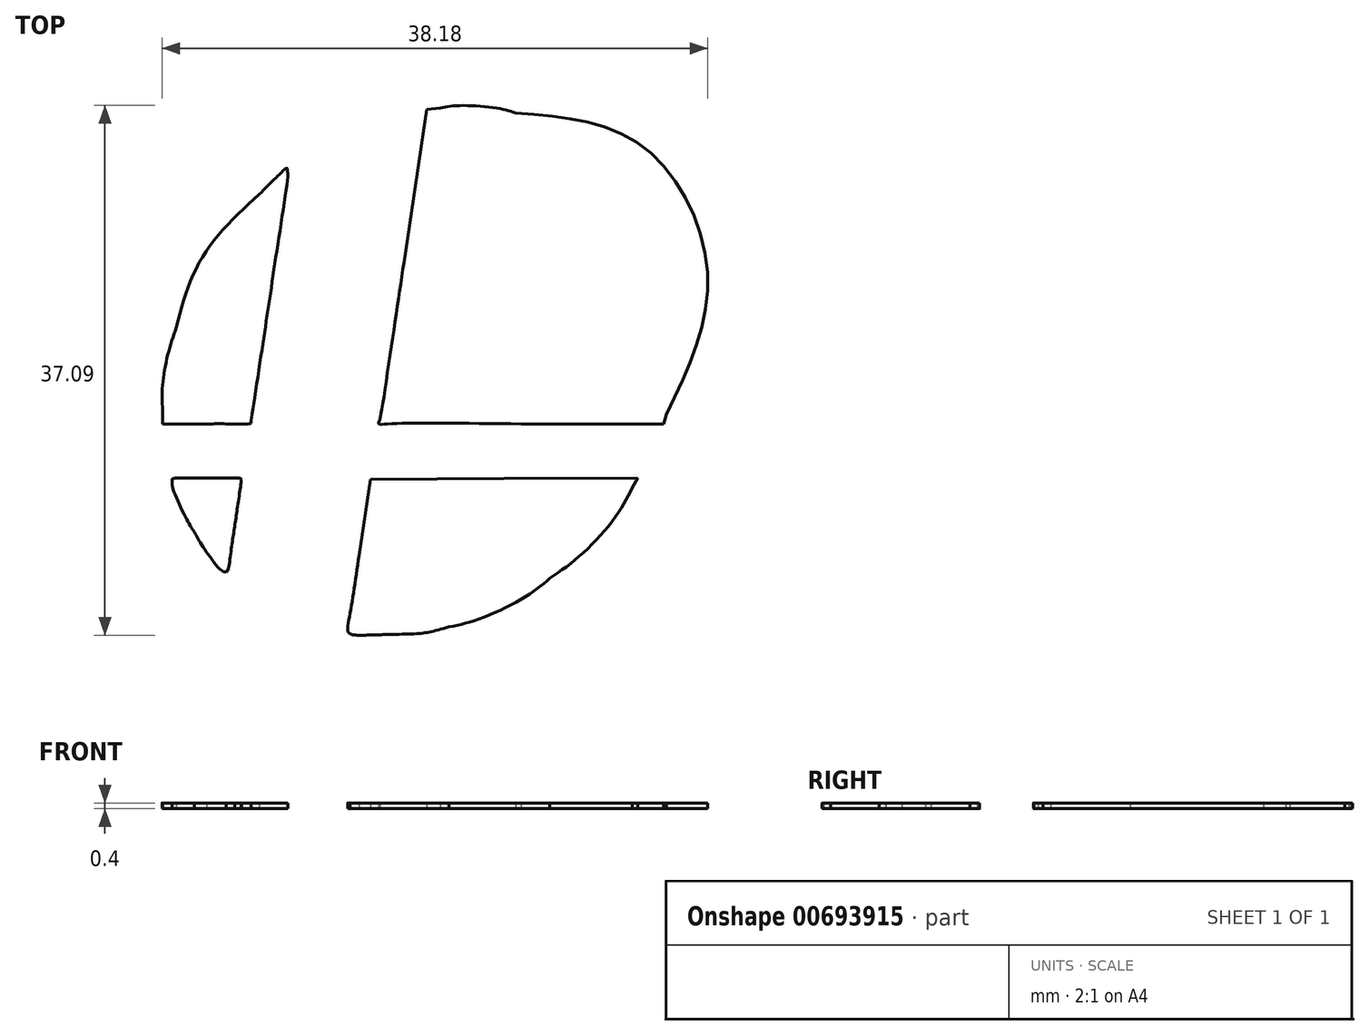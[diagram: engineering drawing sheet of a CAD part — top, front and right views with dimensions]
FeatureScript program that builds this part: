
annotation { "Feature Type Name" : "Feature", "Feature Type Description" : "" }
export const myFeature = defineFeature(function(context is Context, id is Id, definition is map)
    precondition{}
    {
        {
            var Q0;
            Q0=qCreatedBy(makeId("Top.planeOp"),FACE);
            var sketch = newSketch(context, id + "F0", { "sketchPlane" : qUnion([Q0])});
            skFitSpline(sketch, "E0", {"points": [v(-1.5, -38.66) * mm, v(-1.62, -38.6) * mm, v(-1.86, -38.27) * mm, v(-2.05, -37.9) * mm]});
            skFitSpline(sketch, "E1", {"points": [v(-2.05, -37.9) * mm, v(-2.61, -36.8) * mm, v(-4.04, -36.4) * mm, v(-5.38, -36.95) * mm]});
            skFitSpline(sketch, "E2", {"points": [v(-5.38, -36.95) * mm, v(-6.21, -37.3) * mm, v(-7.38, -37.27) * mm, v(-8.93, -36.87) * mm]});
            skFitSpline(sketch, "E3", {"points": [v(-8.93, -36.87) * mm, v(-9.64, -36.68) * mm, v(-10.67, -36.53) * mm, v(-11.21, -36.53) * mm]});
            skFitSpline(sketch, "E4", {"points": [v(-12.1, -36) * mm, v(-11.96, -35.34) * mm, v(-12.11, -35.34) * mm, v(-14.25, -36) * mm]});
            skFitSpline(sketch, "E5", {"points": [v(-14.25, -36) * mm, v(-16.51, -36.7) * mm, v(-18.19, -36.93) * mm, v(-20, -36.8) * mm]});
            skFitSpline(sketch, "E6", {"points": [v(-20, -36.8) * mm, v(-21.86, -36.67) * mm, v(-23.16, -36.25) * mm, v(-24.98, -35.16) * mm]});
            skFitSpline(sketch, "E7", {"points": [v(-24.98, -35.16) * mm, v(-25.76, -34.7) * mm, v(-26.77, -34.22) * mm, v(-27.22, -34.1) * mm]});
            skFitSpline(sketch, "E8", {"points": [v(-27.22, -34.1) * mm, v(-28.1, -33.89) * mm, v(-28.19, -33.77) * mm, v(-27.78, -33.43) * mm]});
            skFitSpline(sketch, "E9", {"points": [v(-27.78, -33.43) * mm, v(-27.64, -33.3) * mm, v(-27.52, -33.16) * mm, v(-27.52, -33.1) * mm]});
            skFitSpline(sketch, "E10", {"points": [v(-27.52, -33.1) * mm, v(-27.52, -33.02) * mm, v(-28.28, -32.84) * mm, v(-29.22, -32.69) * mm]});
            skFitSpline(sketch, "E11", {"points": [v(-29.22, -32.69) * mm, v(-31.36, -32.34) * mm, v(-32.5, -31.83) * mm, v(-33.76, -30.68) * mm]});
            skFitSpline(sketch, "E12", {"points": [v(-33.76, -30.68) * mm, v(-35.5, -29.09) * mm, v(-36.12, -27.5) * mm, v(-35.53, -26.12) * mm]});
            skFitSpline(sketch, "E13", {"points": [v(-35.53, -26.12) * mm, v(-35.27, -25.47) * mm, v(-35.27, -25.42) * mm, v(-35.58, -25) * mm]});
            skFitSpline(sketch, "E14", {"points": [v(-35.58, -25) * mm, v(-36.12, -24.27) * mm, v(-36.64, -23.14) * mm, v(-36.64, -22.72) * mm]});
            skFitSpline(sketch, "E15", {"points": [v(-36.64, -22.72) * mm, v(-36.64, -22.5) * mm, v(-36.52, -22.15) * mm, v(-36.37, -21.93) * mm]});
            skFitSpline(sketch, "E16", {"points": [v(-36.37, -21.93) * mm, v(-36.03, -21.45) * mm, v(-36.13, -21.3) * mm, v(-37.15, -20.78) * mm]});
            skFitSpline(sketch, "E17", {"points": [v(-37.15, -20.78) * mm, v(-38.12, -20.29) * mm, v(-39, -19.3) * mm, v(-39.22, -18.45) * mm]});
            skFitSpline(sketch, "E18", {"points": [v(-39.22, -18.45) * mm, v(-39.36, -17.88) * mm, v(-39.67, -15.62) * mm, v(-39.85, -13.7) * mm]});
            skLineSegment(sketch, "E19", {"start": v(-11.21, -36.53) * mm, "end": v(-12.2, -36.52) * mm});
            skLineSegment(sketch, "E20", {"start": v(-12.2, -36.52) * mm, "end": v(-12.1, -36) * mm});
            skFitSpline(sketch, "E21", {"points": [v(-39.4, -12.9) * mm, v(-38.76, -13) * mm, v(-38.4, -12.74) * mm, v(-38.22, -12.03) * mm]});
            skFitSpline(sketch, "E22", {"points": [v(-38.22, -12.03) * mm, v(-38.1, -11.58) * mm, v(-37.97, -11.47) * mm, v(-37.4, -11.36) * mm]});
            skFitSpline(sketch, "E23", {"points": [v(-37.4, -11.36) * mm, v(-36.15, -11.1) * mm, v(-36.04, -10.46) * mm, v(-36.72, -7.13) * mm]});
            skFitSpline(sketch, "E24", {"points": [v(-36.72, -7.13) * mm, v(-37.48, -3.42) * mm, v(-37.47, -0.76) * mm, v(-36.7, 0.41) * mm]});
            skLineSegment(sketch, "E25", {"start": v(-39.85, -13.7) * mm, "end": v(-39.94, -12.83) * mm});
            skLineSegment(sketch, "E26", {"start": v(-39.94, -12.83) * mm, "end": v(-39.4, -12.9) * mm});
            skFitSpline(sketch, "E27", {"points": [v(-36.25, 0.32) * mm, v(-36.14, -0.12) * mm, v(-36.03, -0.22) * mm, v(-35.73, -0.18) * mm]});
            skFitSpline(sketch, "E28", {"points": [v(-35.73, -0.18) * mm, v(-35.16, -0.1) * mm, v(-34.73, 0.95) * mm, v(-34.62, 2.55) * mm]});
            skFitSpline(sketch, "E29", {"points": [v(-34.62, 2.55) * mm, v(-34.57, 3.3) * mm, v(-34.48, 3.9) * mm, v(-34.42, 3.87) * mm]});
            skFitSpline(sketch, "E30", {"points": [v(-34.42, 3.87) * mm, v(-33.43, 3.32) * mm, v(-32.93, 3.2) * mm, v(-32.28, 3.4) * mm]});
            skFitSpline(sketch, "E31", {"points": [v(-32.28, 3.4) * mm, v(-30.88, 3.82) * mm, v(-28.76, 6.37) * mm, v(-28.4, 8.06) * mm]});
            skFitSpline(sketch, "E32", {"points": [v(-28.4, 8.06) * mm, v(-28.18, 9.04) * mm, v(-28.44, 9.93) * mm, v(-29.04, 10.3) * mm]});
            skFitSpline(sketch, "E33", {"points": [v(-29.04, 10.3) * mm, v(-29.36, 10.5) * mm, v(-29.37, 10.57) * mm, v(-29.14, 11.13) * mm]});
            skFitSpline(sketch, "E34", {"points": [v(-29.14, 11.13) * mm, v(-29.01, 11.47) * mm, v(-28.66, 12.56) * mm, v(-28.37, 13.55) * mm]});
            skFitSpline(sketch, "E35", {"points": [v(-28.37, 13.55) * mm, v(-28.08, 14.55) * mm, v(-27.62, 15.71) * mm, v(-27.34, 16.14) * mm]});
            skFitSpline(sketch, "E36", {"points": [v(-27.34, 16.14) * mm, v(-26.85, 16.9) * mm, v(-25.28, 18.56) * mm, v(-25.28, 18.31) * mm]});
            skFitSpline(sketch, "E37", {"points": [v(-25.28, 18.31) * mm, v(-25.28, 18.24) * mm, v(-25.4, 17.8) * mm, v(-25.56, 17.32) * mm]});
            skFitSpline(sketch, "E38", {"points": [v(-25.56, 17.32) * mm, v(-25.91, 16.25) * mm, v(-25.8, 15.03) * mm, v(-25.31, 14.54) * mm]});
            skFitSpline(sketch, "E39", {"points": [v(-25.31, 14.54) * mm, v(-24.47, 13.7) * mm, v(-21.96, 14.42) * mm, v(-20.69, 15.86) * mm]});
            skFitSpline(sketch, "E40", {"points": [v(-20.69, 15.86) * mm, v(-20.33, 16.27) * mm, v(-19.57, 17.49) * mm, v(-19, 18.56) * mm]});
            skFitSpline(sketch, "E41", {"points": [v(-19, 18.56) * mm, v(-17.86, 20.73) * mm, v(-16.65, 22.12) * mm, v(-15.24, 22.9) * mm]});
            skFitSpline(sketch, "E42", {"points": [v(-15.24, 22.9) * mm, v(-14.78, 23.16) * mm, v(-14.37, 23.36) * mm, v(-14.34, 23.36) * mm]});
            skFitSpline(sketch, "E43", {"points": [v(-14.34, 23.36) * mm, v(-14.3, 23.36) * mm, v(-14.44, 23.1) * mm, v(-14.63, 22.76) * mm]});
            skFitSpline(sketch, "E44", {"points": [v(-14.63, 22.76) * mm, v(-15.12, 21.94) * mm, v(-15.1, 20.92) * mm, v(-14.55, 19.56) * mm]});
            skFitSpline(sketch, "E45", {"points": [v(-14.55, 19.56) * mm, v(-14, 18.2) * mm, v(-13.98, 17.3) * mm, v(-14.45, 16.1) * mm]});
            skFitSpline(sketch, "E46", {"points": [v(-14.45, 16.1) * mm, v(-14.68, 15.54) * mm, v(-14.76, 15.05) * mm, v(-14.7, 14.77) * mm]});
            skFitSpline(sketch, "E47", {"points": [v(-14.7, 14.77) * mm, v(-14.58, 14.36) * mm, v(-14.56, 14.38) * mm, v(-14.34, 15.1) * mm]});
            skFitSpline(sketch, "E48", {"points": [v(-14.34, 15.1) * mm, v(-14.2, 15.59) * mm, v(-13.89, 16.05) * mm, v(-13.5, 16.39) * mm]});
            skFitSpline(sketch, "E49", {"points": [v(-13.5, 16.39) * mm, v(-13.15, 16.68) * mm, v(-12.77, 17.22) * mm, v(-12.63, 17.6) * mm]});
            skLineSegment(sketch, "E50", {"start": v(-36.7, 0.41) * mm, "end": v(-36.4, 0.87) * mm});
            skLineSegment(sketch, "E51", {"start": v(-36.4, 0.87) * mm, "end": v(-36.25, 0.32) * mm});
            skFitSpline(sketch, "E52", {"points": [v(-12.38, 17.11) * mm, v(-12.38, 16.46) * mm, v(-12.5, 15.46) * mm, v(-12.66, 14.87) * mm]});
            skFitSpline(sketch, "E53", {"points": [v(-12.66, 14.87) * mm, v(-13.02, 13.5) * mm, v(-12.8, 12.48) * mm, v(-12.03, 12.1) * mm]});
            skFitSpline(sketch, "E54", {"points": [v(-12.03, 12.1) * mm, v(-11.76, 11.95) * mm, v(-11.5, 11.83) * mm, v(-11.44, 11.83) * mm]});
            skFitSpline(sketch, "E55", {"points": [v(-11.44, 11.83) * mm, v(-11.39, 11.83) * mm, v(-11.34, 12.22) * mm, v(-11.34, 12.68) * mm]});
            skFitSpline(sketch, "E56", {"points": [v(-11.34, 12.68) * mm, v(-11.34, 13.78) * mm, v(-11.12, 14.35) * mm, v(-10.4, 15.05) * mm]});
            skFitSpline(sketch, "E57", {"points": [v(-10.4, 15.05) * mm, v(-9.7, 15.73) * mm, v(-9.65, 16.08) * mm, v(-9.92, 18.2) * mm]});
            skFitSpline(sketch, "E58", {"points": [v(-9.92, 18.2) * mm, v(-10.03, 19.1) * mm, v(-10.13, 20.33) * mm, v(-10.13, 20.94) * mm]});
            skFitSpline(sketch, "E59", {"points": [v(-10.13, 20.94) * mm, v(-10.14, 21.93) * mm, v(-10.07, 22.17) * mm, v(-9.46, 23.18) * mm]});
            skFitSpline(sketch, "E60", {"points": [v(-9.46, 23.18) * mm, v(-8.57, 24.68) * mm, v(-8.51, 25.02) * mm, v(-9.2, 24.94) * mm]});
            skFitSpline(sketch, "E61", {"points": [v(-9.2, 24.94) * mm, v(-9.9, 24.87) * mm, v(-10.4, 24.52) * mm, v(-11.01, 23.66) * mm]});
            skLineSegment(sketch, "E62", {"start": v(-12.63, 17.6) * mm, "end": v(-12.4, 18.29) * mm});
            skLineSegment(sketch, "E63", {"start": v(-12.4, 18.29) * mm, "end": v(-12.38, 17.11) * mm});
            skFitSpline(sketch, "E64", {"points": [v(-11.42, 24.14) * mm, v(-11.19, 26.66) * mm, v(-10.74, 27.64) * mm, v(-8.77, 29.86) * mm]});
            skFitSpline(sketch, "E65", {"points": [v(-8.77, 29.86) * mm, v(-8, 30.74) * mm, v(-7.34, 31.45) * mm, v(-7.3, 31.45) * mm]});
            skFitSpline(sketch, "E66", {"points": [v(-7.3, 31.45) * mm, v(-7.26, 31.45) * mm, v(-7.35, 31.18) * mm, v(-7.49, 30.84) * mm]});
            skFitSpline(sketch, "E67", {"points": [v(-7.49, 30.84) * mm, v(-7.63, 30.5) * mm, v(-7.7, 30.16) * mm, v(-7.64, 30.07) * mm]});
            skFitSpline(sketch, "E68", {"points": [v(-7.64, 30.07) * mm, v(-7.27, 29.47) * mm, v(-5.55, 30.5) * mm, v(-4.96, 31.67) * mm]});
            skFitSpline(sketch, "E69", {"points": [v(-4.96, 31.67) * mm, v(-4, 33.55) * mm, v(-2.7, 34.97) * mm, v(-1.21, 35.75) * mm]});
            skLineSegment(sketch, "E70", {"start": v(-11.01, 23.66) * mm, "end": v(-11.53, 22.94) * mm});
            skLineSegment(sketch, "E71", {"start": v(-11.53, 22.94) * mm, "end": v(-11.42, 24.14) * mm});
            skFitSpline(sketch, "E72", {"points": [v(-1.23, 35.39) * mm, v(-1.47, 35.07) * mm, v(-1.76, 34.62) * mm, v(-1.88, 34.4) * mm]});
            skFitSpline(sketch, "E73", {"points": [v(-1.88, 34.4) * mm, v(-2.08, 34) * mm, v(-2.07, 34) * mm, v(-1.6, 34.11) * mm]});
            skLineSegment(sketch, "E74", {"start": v(-1.21, 35.75) * mm, "end": v(-0.8, 35.96) * mm});
            skLineSegment(sketch, "E75", {"start": v(-0.8, 35.96) * mm, "end": v(-1.23, 35.39) * mm});
            skFitSpline(sketch, "E76", {"points": [v(-1.47, 33.83) * mm, v(-2.74, 32.41) * mm, v(-1.79, 32.96) * mm, v(0.05, 34.7) * mm]});
            skFitSpline(sketch, "E77", {"points": [v(0.05, 34.7) * mm, v(0.88, 35.49) * mm, v(1.75, 36.52) * mm, v(2.12, 37.15) * mm]});
            skLineSegment(sketch, "E78", {"start": v(-1.6, 34.11) * mm, "end": v(-1.1, 34.23) * mm});
            skLineSegment(sketch, "E79", {"start": v(-1.1, 34.23) * mm, "end": v(-1.47, 33.83) * mm});
            skFitSpline(sketch, "E80", {"points": [v(2.77, 36.92) * mm, v(2.77, 34.91) * mm, v(2.38, 34.08) * mm, v(0.51, 32.04) * mm]});
            skFitSpline(sketch, "E81", {"points": [v(0.51, 32.04) * mm, v(-1.75, 29.57) * mm, v(-2.86, 28.17) * mm, v(-3.24, 27.3) * mm]});
            skFitSpline(sketch, "E82", {"points": [v(-3.24, 27.3) * mm, v(-3.76, 26.12) * mm, v(-3.77, 25.43) * mm, v(-3.27, 25.43) * mm]});
            skFitSpline(sketch, "E83", {"points": [v(-3.27, 25.43) * mm, v(-2.77, 25.43) * mm, v(-2.02, 26.42) * mm, v(-1.46, 27.8) * mm]});
            skLineSegment(sketch, "E84", {"start": v(2.12, 37.15) * mm, "end": v(2.77, 38.24) * mm});
            skLineSegment(sketch, "E85", {"start": v(2.77, 38.24) * mm, "end": v(2.77, 36.92) * mm});
            skFitSpline(sketch, "E86", {"points": [v(-0.74, 28.53) * mm, v(-0.6, 28.21) * mm, v(-0.4, 28.01) * mm, v(-0.2, 28.01) * mm]});
            skFitSpline(sketch, "E87", {"points": [v(-0.2, 28.01) * mm, v(0.33, 28.01) * mm, v(1.4, 28.9) * mm, v(2.41, 30.13) * mm]});
            skFitSpline(sketch, "E88", {"points": [v(2.41, 30.13) * mm, v(2.93, 30.76) * mm, v(3.37, 31.28) * mm, v(3.4, 31.28) * mm]});
            skFitSpline(sketch, "E89", {"points": [v(3.4, 31.28) * mm, v(3.42, 31.28) * mm, v(3.25, 30.78) * mm, v(3.02, 30.16) * mm]});
            skFitSpline(sketch, "E90", {"points": [v(3.02, 30.16) * mm, v(2.56, 28.93) * mm, v(2.48, 28.25) * mm, v(2.8, 28.14) * mm]});
            skFitSpline(sketch, "E91", {"points": [v(2.8, 28.14) * mm, v(3.27, 27.99) * mm, v(1.8, 25.16) * mm, v(0.4, 23.54) * mm]});
            skFitSpline(sketch, "E92", {"points": [v(0.4, 23.54) * mm, v(0, 23.08) * mm, v(-0.98, 22.22) * mm, v(-1.78, 21.64) * mm]});
            skFitSpline(sketch, "E93", {"points": [v(-1.78, 21.64) * mm, v(-2.89, 20.84) * mm, v(-3.29, 20.43) * mm, v(-3.5, 19.9) * mm]});
            skFitSpline(sketch, "E94", {"points": [v(-3.5, 19.9) * mm, v(-3.85, 19.04) * mm, v(-3.87, 17.51) * mm, v(-3.53, 17.51) * mm]});
            skFitSpline(sketch, "E95", {"points": [v(-3.53, 17.51) * mm, v(-3.2, 17.51) * mm, v(-2.62, 18.03) * mm, v(-2.3, 18.63) * mm]});
            skLineSegment(sketch, "E96", {"start": v(-1.46, 27.8) * mm, "end": v(-0.96, 29.06) * mm});
            skLineSegment(sketch, "E97", {"start": v(-0.96, 29.06) * mm, "end": v(-0.74, 28.53) * mm});
            skFitSpline(sketch, "E98", {"points": [v(-2.12, 18.33) * mm, v(-2.23, 17.4) * mm, v(-2.5, 16.8) * mm, v(-3.38, 15.5) * mm]});
            skFitSpline(sketch, "E99", {"points": [v(-3.38, 15.5) * mm, v(-4.52, 13.82) * mm, v(-3.7, 13.38) * mm, v(-1.81, 14.68) * mm]});
            skFitSpline(sketch, "E100", {"points": [v(-1.81, 14.68) * mm, v(-0.75, 15.4) * mm, v(0.32, 15.96) * mm, v(0.65, 15.96) * mm]});
            skFitSpline(sketch, "E101", {"points": [v(0.65, 15.96) * mm, v(0.72, 15.96) * mm, v(0.5, 15.67) * mm, v(0.15, 15.32) * mm]});
            skFitSpline(sketch, "E102", {"points": [v(0.15, 15.32) * mm, v(-0.5, 14.65) * mm, v(-1.16, 13.45) * mm, v(-1.54, 12.26) * mm]});
            skFitSpline(sketch, "E103", {"points": [v(-1.54, 12.26) * mm, v(-1.86, 11.26) * mm, v(-2.58, 10.29) * mm, v(-3.9, 9.1) * mm]});
            skLineSegment(sketch, "E104", {"start": v(-2.3, 18.63) * mm, "end": v(-2.02, 19.15) * mm});
            skLineSegment(sketch, "E105", {"start": v(-2.02, 19.15) * mm, "end": v(-2.12, 18.33) * mm});
            skFitSpline(sketch, "E106", {"points": [v(-4.23, 8.39) * mm, v(-3.16, 8.84) * mm, v(-1, 10.32) * mm, v(0, 11.32) * mm]});
            skFitSpline(sketch, "E107", {"points": [v(0, 11.32) * mm, v(1.25, 12.53) * mm, v(1.9, 14.34) * mm, v(1.9, 16.53) * mm]});
            skFitSpline(sketch, "E108", {"points": [v(1.9, 16.53) * mm, v(1.9, 17) * mm, v(2, 17.7) * mm, v(2.12, 18.1) * mm]});
            skFitSpline(sketch, "E109", {"points": [v(2.12, 18.1) * mm, v(2.36, 18.92) * mm, v(3.71, 20.37) * mm, v(4.4, 20.54) * mm]});
            skFitSpline(sketch, "E110", {"points": [v(4.4, 20.54) * mm, v(4.7, 20.62) * mm, v(4.97, 20.9) * mm, v(5.26, 21.46) * mm]});
            skFitSpline(sketch, "E111", {"points": [v(5.26, 21.46) * mm, v(5.8, 22.51) * mm, v(6.7, 23.32) * mm, v(8.2, 24.06) * mm]});
            skFitSpline(sketch, "E112", {"points": [v(8.2, 24.06) * mm, v(10.3, 25.1) * mm, v(11.51, 26.57) * mm, v(12.88, 29.73) * mm]});
            skFitSpline(sketch, "E113", {"points": [v(12.88, 29.73) * mm, v(13.05, 30.1) * mm, v(13.07, 30.03) * mm, v(13.08, 29.14) * mm]});
            skFitSpline(sketch, "E114", {"points": [v(13.08, 29.14) * mm, v(13.09, 28.58) * mm, v(13, 27.63) * mm, v(12.9, 27.03) * mm]});
            skFitSpline(sketch, "E115", {"points": [v(12.9, 27.03) * mm, v(12.8, 26.42) * mm, v(12.76, 25.88) * mm, v(12.82, 25.81) * mm]});
            skFitSpline(sketch, "E116", {"points": [v(12.82, 25.81) * mm, v(12.89, 25.75) * mm, v(13.1, 25.8) * mm, v(13.32, 25.93) * mm]});
            skFitSpline(sketch, "E117", {"points": [v(13.32, 25.93) * mm, v(13.68, 26.16) * mm, v(13.69, 26.15) * mm, v(13.4, 25.83) * mm]});
            skFitSpline(sketch, "E118", {"points": [v(13.4, 25.83) * mm, v(12.94, 25.32) * mm, v(12.6, 24.36) * mm, v(12.7, 23.86) * mm]});
            skFitSpline(sketch, "E119", {"points": [v(12.7, 23.86) * mm, v(12.82, 23.19) * mm, v(12.38, 22.65) * mm, v(11.07, 21.89) * mm]});
            skFitSpline(sketch, "E120", {"points": [v(11.07, 21.89) * mm, v(9.08, 20.73) * mm, v(8.23, 19.79) * mm, v(7.92, 18.4) * mm]});
            skFitSpline(sketch, "E121", {"points": [v(7.92, 18.4) * mm, v(7.84, 18.07) * mm, v(7.86, 17.62) * mm, v(7.95, 17.38) * mm]});
            skFitSpline(sketch, "E122", {"points": [v(7.95, 17.38) * mm, v(8.1, 16.99) * mm, v(8.18, 16.96) * mm, v(8.97, 17.04) * mm]});
            skFitSpline(sketch, "E123", {"points": [v(8.97, 17.04) * mm, v(10.1, 17.14) * mm, v(10.08, 16.93) * mm, v(8.88, 16.07) * mm]});
            skFitSpline(sketch, "E124", {"points": [v(8.88, 16.07) * mm, v(8.3, 15.66) * mm, v(8.7, 15.57) * mm, v(9.77, 15.88) * mm]});
            skFitSpline(sketch, "E125", {"points": [v(9.77, 15.88) * mm, v(11.34, 16.33) * mm, v(11.77, 16.77) * mm, v(12.92, 19.05) * mm]});
            skFitSpline(sketch, "E126", {"points": [v(12.92, 19.05) * mm, v(13.47, 20.17) * mm, v(14.19, 21.33) * mm, v(14.5, 21.65) * mm]});
            skFitSpline(sketch, "E127", {"points": [v(14.5, 21.65) * mm, v(15.05, 22.2) * mm, v(16.82, 23.14) * mm, v(16.98, 22.98) * mm]});
            skFitSpline(sketch, "E128", {"points": [v(16.98, 22.98) * mm, v(17.03, 22.93) * mm, v(16.78, 22.68) * mm, v(16.44, 22.42) * mm]});
            skFitSpline(sketch, "E129", {"points": [v(16.44, 22.42) * mm, v(15.8, 21.94) * mm, v(15.16, 20.81) * mm, v(15.17, 20.18) * mm]});
            skFitSpline(sketch, "E130", {"points": [v(15.17, 20.18) * mm, v(15.17, 19.88) * mm, v(15.22, 19.9) * mm, v(15.62, 20.34) * mm]});
            skLineSegment(sketch, "E131", {"start": v(-3.9, 9.1) * mm, "end": v(-5.06, 8.04) * mm});
            skLineSegment(sketch, "E132", {"start": v(-5.06, 8.04) * mm, "end": v(-4.23, 8.39) * mm});
            skFitSpline(sketch, "E133", {"points": [v(15.94, 20.08) * mm, v(15.88, 19.66) * mm, v(15.55, 18.72) * mm, v(15.22, 17.98) * mm]});
            skFitSpline(sketch, "E134", {"points": [v(15.22, 17.98) * mm, v(14.56, 16.55) * mm, v(14.56, 16.04) * mm, v(15.2, 16.23) * mm]});
            skFitSpline(sketch, "E135", {"points": [v(15.2, 16.23) * mm, v(16.13, 16.5) * mm, v(18.1, 17.84) * mm, v(19.2, 18.96) * mm]});
            skFitSpline(sketch, "E136", {"points": [v(19.2, 18.96) * mm, v(20.48, 20.24) * mm, v(21, 21.11) * mm, v(21.87, 23.46) * mm]});
            skFitSpline(sketch, "E137", {"points": [v(21.87, 23.46) * mm, v(22.48, 25.1) * mm, v(23.37, 26.61) * mm, v(24.48, 27.89) * mm]});
            skFitSpline(sketch, "E138", {"points": [v(24.48, 27.89) * mm, v(25.3, 28.82) * mm, v(26.63, 29.65) * mm, v(28.56, 30.41) * mm]});
            skLineSegment(sketch, "E139", {"start": v(15.62, 20.34) * mm, "end": v(16.06, 20.85) * mm});
            skLineSegment(sketch, "E140", {"start": v(16.06, 20.85) * mm, "end": v(15.94, 20.08) * mm});
            skFitSpline(sketch, "E141", {"points": [v(28.07, 29.45) * mm, v(26.54, 28) * mm, v(25.66, 26.69) * mm, v(25.66, 25.83) * mm]});
            skFitSpline(sketch, "E142", {"points": [v(25.66, 25.83) * mm, v(25.66, 25.22) * mm, v(25.9, 25.06) * mm, v(26.48, 25.28) * mm]});
            skFitSpline(sketch, "E143", {"points": [v(26.48, 25.28) * mm, v(26.88, 25.43) * mm, v(26.88, 25.43) * mm, v(26.58, 24.93) * mm]});
            skFitSpline(sketch, "E144", {"points": [v(26.58, 24.93) * mm, v(26.42, 24.65) * mm, v(25.91, 23.99) * mm, v(25.46, 23.45) * mm]});
            skFitSpline(sketch, "E145", {"points": [v(25.46, 23.45) * mm, v(24.53, 22.36) * mm, v(24.38, 21.72) * mm, v(25.01, 21.49) * mm]});
            skFitSpline(sketch, "E146", {"points": [v(25.01, 21.49) * mm, v(25.22, 21.4) * mm, v(25.5, 21.38) * mm, v(25.63, 21.43) * mm]});
            skFitSpline(sketch, "E147", {"points": [v(25.63, 21.43) * mm, v(25.81, 21.5) * mm, v(25.84, 21.42) * mm, v(25.74, 21.1) * mm]});
            skFitSpline(sketch, "E148", {"points": [v(25.74, 21.1) * mm, v(25.27, 19.59) * mm, v(24.19, 18.3) * mm, v(22.25, 16.98) * mm]});
            skFitSpline(sketch, "E149", {"points": [v(22.25, 16.98) * mm, v(20.48, 15.77) * mm, v(18.77, 14.42) * mm, v(18.77, 14.23) * mm]});
            skFitSpline(sketch, "E150", {"points": [v(18.77, 14.23) * mm, v(18.77, 14.04) * mm, v(19.3, 14.24) * mm, v(21.27, 15.18) * mm]});
            skFitSpline(sketch, "E151", {"points": [v(21.27, 15.18) * mm, v(23.73, 16.37) * mm, v(26.39, 18.5) * mm, v(28.46, 20.95) * mm]});
            skLineSegment(sketch, "E152", {"start": v(28.56, 30.41) * mm, "end": v(29.48, 30.77) * mm});
            skLineSegment(sketch, "E153", {"start": v(29.48, 30.77) * mm, "end": v(28.07, 29.45) * mm});
            skFitSpline(sketch, "E154", {"points": [v(29, 21.04) * mm, v(28.29, 18.62) * mm, v(26.38, 15.51) * mm, v(24.49, 13.7) * mm]});
            skFitSpline(sketch, "E155", {"points": [v(24.49, 13.7) * mm, v(22.48, 11.77) * mm, v(19.35, 9.85) * mm, v(17.62, 9.49) * mm]});
            skFitSpline(sketch, "E156", {"points": [v(17.62, 9.49) * mm, v(15.9, 9.13) * mm, v(14.89, 8.6) * mm, v(12.75, 7) * mm]});
            skFitSpline(sketch, "E157", {"points": [v(12.75, 7) * mm, v(10.24, 5.1) * mm, v(9.92, 4.82) * mm, v(9.4, 4.1) * mm]});
            skFitSpline(sketch, "E158", {"points": [v(9.4, 4.1) * mm, v(8.9, 3.41) * mm, v(8.85, 3.02) * mm, v(9.23, 2.64) * mm]});
            skFitSpline(sketch, "E159", {"points": [v(9.23, 2.64) * mm, v(9.82, 2.05) * mm, v(12.51, 2.58) * mm, v(14.98, 3.76) * mm]});
            skFitSpline(sketch, "E160", {"points": [v(14.98, 3.76) * mm, v(16.23, 4.35) * mm, v(16.67, 4.7) * mm, v(18.1, 6.16) * mm]});
            skLineSegment(sketch, "E161", {"start": v(28.46, 20.95) * mm, "end": v(29.26, 21.9) * mm});
            skLineSegment(sketch, "E162", {"start": v(29.26, 21.9) * mm, "end": v(29, 21.04) * mm});
            skFitSpline(sketch, "E163", {"points": [v(20.85, 7.2) * mm, v(20.4, 6.75) * mm, v(20.08, 6.21) * mm, v(19.9, 5.62) * mm]});
            skFitSpline(sketch, "E164", {"points": [v(19.9, 5.62) * mm, v(19.57, 4.5) * mm, v(19.57, 4.24) * mm, v(19.88, 3.82) * mm]});
            skFitSpline(sketch, "E165", {"points": [v(19.88, 3.82) * mm, v(20.1, 3.53) * mm, v(20.18, 3.52) * mm, v(20.5, 3.71) * mm]});
            skFitSpline(sketch, "E166", {"points": [v(20.5, 3.71) * mm, v(20.84, 3.92) * mm, v(20.86, 3.91) * mm, v(20.74, 3.54) * mm]});
            skFitSpline(sketch, "E167", {"points": [v(20.74, 3.54) * mm, v(20.46, 2.61) * mm, v(19.99, 2) * mm, v(18.02, 0) * mm]});
            skFitSpline(sketch, "E168", {"points": [v(18.02, 0) * mm, v(16.55, -1.5) * mm, v(15.87, -2.08) * mm, v(15.68, -2) * mm]});
            skFitSpline(sketch, "E169", {"points": [v(15.68, -2) * mm, v(14.7, -1.6) * mm, v(13.92, -1.57) * mm, v(12.79, -1.91) * mm]});
            skFitSpline(sketch, "E170", {"points": [v(12.79, -1.91) * mm, v(10.78, -2.52) * mm, v(9.3, -3.74) * mm, v(9.3, -4.79) * mm]});
            skFitSpline(sketch, "E171", {"points": [v(9.3, -4.79) * mm, v(9.3, -4.98) * mm, v(9.1, -5.33) * mm, v(8.86, -5.56) * mm]});
            skFitSpline(sketch, "E172", {"points": [v(8.86, -5.56) * mm, v(8.32, -6.06) * mm, v(7.93, -6.78) * mm, v(7.93, -7.26) * mm]});
            skFitSpline(sketch, "E173", {"points": [v(7.93, -7.26) * mm, v(7.93, -7.68) * mm, v(8.49, -8.05) * mm, v(9.36, -8.2) * mm]});
            skLineSegment(sketch, "E174", {"start": v(18.1, 6.16) * mm, "end": v(19.75, 7.88) * mm});
            skLineSegment(sketch, "E175", {"start": v(19.75, 7.88) * mm, "end": v(20.64, 7.88) * mm});
            skLineSegment(sketch, "E176", {"start": v(20.64, 7.88) * mm, "end": v(21.53, 7.88) * mm});
            skLineSegment(sketch, "E177", {"start": v(21.53, 7.88) * mm, "end": v(20.85, 7.2) * mm});
            skFitSpline(sketch, "E178", {"points": [v(9, -9.08) * mm, v(8, -9.83) * mm, v(7.2, -10.79) * mm, v(7, -11.53) * mm]});
            skFitSpline(sketch, "E179", {"points": [v(7, -11.53) * mm, v(6.9, -11.8) * mm, v(7, -12.03) * mm, v(7.33, -12.37) * mm]});
            skFitSpline(sketch, "E180", {"points": [v(7.33, -12.37) * mm, v(7.77, -12.8) * mm, v(7.84, -12.82) * mm, v(9.28, -12.73) * mm]});
            skFitSpline(sketch, "E181", {"points": [v(9.28, -12.73) * mm, v(11, -12.64) * mm, v(13.11, -11.99) * mm, v(15.62, -10.8) * mm]});
            skFitSpline(sketch, "E182", {"points": [v(15.62, -10.8) * mm, v(18.1, -9.63) * mm, v(19.58, -8.59) * mm, v(21.28, -6.83) * mm]});
            skFitSpline(sketch, "E183", {"points": [v(21.28, -6.83) * mm, v(22.9, -5.15) * mm, v(24.17, -4.35) * mm, v(25.23, -4.35) * mm]});
            skLineSegment(sketch, "E184", {"start": v(9.36, -8.2) * mm, "end": v(10, -8.32) * mm});
            skLineSegment(sketch, "E185", {"start": v(10, -8.32) * mm, "end": v(9, -9.08) * mm});
            skFitSpline(sketch, "E186", {"points": [v(25.22, -4.66) * mm, v(24.52, -5.1) * mm, v(23.84, -5.92) * mm, v(23.6, -6.65) * mm]});
            skFitSpline(sketch, "E187", {"points": [v(23.6, -6.65) * mm, v(23.47, -7.04) * mm, v(23.26, -7.27) * mm, v(23, -7.34) * mm]});
            skFitSpline(sketch, "E188", {"points": [v(23, -7.34) * mm, v(22.77, -7.4) * mm, v(22.35, -7.64) * mm, v(22.07, -7.87) * mm]});
            skFitSpline(sketch, "E189", {"points": [v(22.07, -7.87) * mm, v(21.17, -8.63) * mm, v(21.02, -9.85) * mm, v(21.85, -9.63) * mm]});
            skFitSpline(sketch, "E190", {"points": [v(21.85, -9.63) * mm, v(22.12, -9.56) * mm, v(22.21, -9.62) * mm, v(22.21, -9.83) * mm]});
            skFitSpline(sketch, "E191", {"points": [v(22.21, -9.83) * mm, v(22.21, -10.2) * mm, v(21.31, -11.66) * mm, v(20.6, -12.4) * mm]});
            skLineSegment(sketch, "E192", {"start": v(25.23, -4.35) * mm, "end": v(25.74, -4.34) * mm});
            skLineSegment(sketch, "E193", {"start": v(25.74, -4.34) * mm, "end": v(25.22, -4.66) * mm});
            skFitSpline(sketch, "E194", {"points": [v(20.95, -12.74) * mm, v(20.52, -13.22) * mm, v(18.52, -14.25) * mm, v(17.53, -14.5) * mm]});
            skFitSpline(sketch, "E195", {"points": [v(17.53, -14.5) * mm, v(15.87, -14.92) * mm, v(14.13, -16.65) * mm, v(14.13, -17.88) * mm]});
            skFitSpline(sketch, "E196", {"points": [v(14.13, -17.88) * mm, v(14.13, -18.35) * mm, v(14.21, -18.5) * mm, v(14.56, -18.63) * mm]});
            skFitSpline(sketch, "E197", {"points": [v(14.56, -18.63) * mm, v(15.12, -18.84) * mm, v(14.96, -19.18) * mm, v(13.88, -20.07) * mm]});
            skFitSpline(sketch, "E198", {"points": [v(13.88, -20.07) * mm, v(12.62, -21.1) * mm, v(12.83, -21.38) * mm, v(14.63, -21.04) * mm]});
            skFitSpline(sketch, "E199", {"points": [v(14.63, -21.04) * mm, v(15.82, -20.81) * mm, v(16.63, -20.41) * mm, v(17.31, -19.7) * mm]});
            skFitSpline(sketch, "E200", {"points": [v(17.31, -19.7) * mm, v(17.92, -19.09) * mm, v(18.66, -18.8) * mm, v(19.65, -18.8) * mm]});
            skFitSpline(sketch, "E201", {"points": [v(19.65, -18.8) * mm, v(20, -18.8) * mm, v(20.6, -18.68) * mm, v(21, -18.54) * mm]});
            skFitSpline(sketch, "E202", {"points": [v(21, -18.54) * mm, v(21.41, -18.4) * mm, v(21.77, -18.28) * mm, v(21.8, -18.28) * mm]});
            skFitSpline(sketch, "E203", {"points": [v(21.8, -18.28) * mm, v(21.85, -18.28) * mm, v(21.57, -18.68) * mm, v(21.19, -19.16) * mm]});
            skFitSpline(sketch, "E204", {"points": [v(21.19, -19.16) * mm, v(20.45, -20.1) * mm, v(20.37, -20.33) * mm, v(20.7, -20.66) * mm]});
            skFitSpline(sketch, "E205", {"points": [v(20.7, -20.66) * mm, v(21.25, -21.21) * mm, v(24.73, -20.48) * mm, v(26.5, -19.44) * mm]});
            skFitSpline(sketch, "E206", {"points": [v(26.5, -19.44) * mm, v(27.02, -19.13) * mm, v(28.73, -17.64) * mm, v(30.31, -16.11) * mm]});
            skFitSpline(sketch, "E207", {"points": [v(30.31, -16.11) * mm, v(33.04, -13.47) * mm, v(34.3, -12.5) * mm, v(35.96, -11.81) * mm]});
            skFitSpline(sketch, "E208", {"points": [v(35.96, -11.81) * mm, v(36.7, -11.5) * mm, v(39.99, -10.53) * mm, v(40.06, -10.6) * mm]});
            skFitSpline(sketch, "E209", {"points": [v(40.06, -10.6) * mm, v(40.09, -10.63) * mm, v(39.32, -11.1) * mm, v(38.35, -11.65) * mm]});
            skFitSpline(sketch, "E210", {"points": [v(38.35, -11.65) * mm, v(35.04, -13.53) * mm, v(33.35, -15.2) * mm, v(33.33, -16.63) * mm]});
            skFitSpline(sketch, "E211", {"points": [v(33.33, -16.63) * mm, v(33.31, -17.43) * mm, v(33.25, -17.4) * mm, v(35.04, -17.18) * mm]});
            skLineSegment(sketch, "E212", {"start": v(20.6, -12.4) * mm, "end": v(20.06, -12.99) * mm});
            skLineSegment(sketch, "E213", {"start": v(20.06, -12.99) * mm, "end": v(20.67, -12.69) * mm});
            skLineSegment(sketch, "E214", {"start": v(20.67, -12.69) * mm, "end": v(21.27, -12.38) * mm});
            skLineSegment(sketch, "E215", {"start": v(21.27, -12.38) * mm, "end": v(20.95, -12.74) * mm});
            skFitSpline(sketch, "E216", {"points": [v(34.7, -18.04) * mm, v(30.38, -21.16) * mm, v(29.58, -21.7) * mm, v(28.3, -22.37) * mm]});
            skFitSpline(sketch, "E217", {"points": [v(28.3, -22.37) * mm, v(27.13, -22.98) * mm, v(25.27, -23.66) * mm, v(22.56, -24.47) * mm]});
            skFitSpline(sketch, "E218", {"points": [v(22.56, -24.47) * mm, v(22.04, -24.62) * mm, v(22.12, -24.63) * mm, v(23.07, -24.55) * mm]});
            skFitSpline(sketch, "E219", {"points": [v(23.07, -24.55) * mm, v(25.73, -24.33) * mm, v(28.55, -23.45) * mm, v(31.85, -21.83) * mm]});
            skLineSegment(sketch, "E220", {"start": v(35.04, -17.18) * mm, "end": v(36.07, -17.04) * mm});
            skLineSegment(sketch, "E221", {"start": v(36.07, -17.04) * mm, "end": v(34.7, -18.04) * mm});
            skFitSpline(sketch, "E222", {"points": [v(32.53, -21.93) * mm, v(30.58, -23.8) * mm, v(27.1, -25.88) * mm, v(24.33, -26.83) * mm]});
            skFitSpline(sketch, "E223", {"points": [v(24.33, -26.83) * mm, v(23.1, -27.25) * mm, v(22.67, -27.3) * mm, v(19.2, -27.41) * mm]});
            skFitSpline(sketch, "E224", {"points": [v(19.2, -27.41) * mm, v(17.08, -27.48) * mm, v(15.11, -27.63) * mm, v(14.73, -27.75) * mm]});
            skFitSpline(sketch, "E225", {"points": [v(14.73, -27.75) * mm, v(14.02, -27.97) * mm, v(12.28, -28.8) * mm, v(11.57, -29.26) * mm]});
            skLineSegment(sketch, "E226", {"start": v(31.85, -21.83) * mm, "end": v(33.49, -21.02) * mm});
            skLineSegment(sketch, "E227", {"start": v(33.49, -21.02) * mm, "end": v(32.53, -21.93) * mm});
            skFitSpline(sketch, "E228", {"points": [v(11.63, -29.77) * mm, v(12.18, -30.06) * mm, v(13.12, -30.08) * mm, v(14.64, -29.83) * mm]});
            skFitSpline(sketch, "E229", {"points": [v(14.64, -29.83) * mm, v(15.26, -29.73) * mm, v(15.83, -29.64) * mm, v(15.91, -29.64) * mm]});
            skFitSpline(sketch, "E230", {"points": [v(15.91, -29.64) * mm, v(16.1, -29.64) * mm, v(14.99, -30.4) * mm, v(14.21, -30.8) * mm]});
            skLineSegment(sketch, "E231", {"start": v(11.57, -29.26) * mm, "end": v(11.17, -29.53) * mm});
            skLineSegment(sketch, "E232", {"start": v(11.17, -29.53) * mm, "end": v(11.63, -29.77) * mm});
            skFitSpline(sketch, "E233", {"points": [v(15.3, -31.05) * mm, v(16.21, -31.02) * mm, v(17.37, -30.93) * mm, v(17.87, -30.86) * mm]});
            skFitSpline(sketch, "E234", {"points": [v(17.87, -30.86) * mm, v(18.37, -30.79) * mm, v(18.77, -30.75) * mm, v(18.77, -30.78) * mm]});
            skFitSpline(sketch, "E235", {"points": [v(18.77, -30.78) * mm, v(18.77, -30.94) * mm, v(17.3, -31.42) * mm, v(15.93, -31.7) * mm]});
            skFitSpline(sketch, "E236", {"points": [v(15.93, -31.7) * mm, v(13.93, -32.12) * mm, v(13.9, -32.14) * mm, v(12.61, -33.11) * mm]});
            skFitSpline(sketch, "E237", {"points": [v(12.61, -33.11) * mm, v(10.67, -34.6) * mm, v(8.97, -34.78) * mm, v(5.87, -33.86) * mm]});
            skFitSpline(sketch, "E238", {"points": [v(5.87, -33.86) * mm, v(3.1, -33.04) * mm, v(1.23, -33.15) * mm, v(0.46, -34.18) * mm]});
            skLineSegment(sketch, "E239", {"start": v(14.21, -30.8) * mm, "end": v(13.62, -31.1) * mm});
            skLineSegment(sketch, "E240", {"start": v(13.62, -31.1) * mm, "end": v(15.3, -31.05) * mm});
            skFitSpline(sketch, "E241", {"points": [v(0.5, -34.99) * mm, v(0.73, -35.17) * mm, v(1.05, -35.32) * mm, v(1.21, -35.32) * mm]});
            skFitSpline(sketch, "E242", {"points": [v(1.21, -35.32) * mm, v(1.38, -35.32) * mm, v(1.8, -35.55) * mm, v(2.17, -35.84) * mm]});
            skFitSpline(sketch, "E243", {"points": [v(2.17, -35.84) * mm, v(2.95, -36.46) * mm, v(3.98, -36.76) * mm, v(4.9, -36.64) * mm]});
            skFitSpline(sketch, "E244", {"points": [v(4.9, -36.64) * mm, v(6.2, -36.47) * mm, v(6.17, -35.84) * mm, v(4.87, -35.83) * mm]});
            skFitSpline(sketch, "E245", {"points": [v(4.87, -35.83) * mm, v(4.08, -35.82) * mm, v(4.07, -35.82) * mm, v(4.49, -35.58) * mm]});
            skFitSpline(sketch, "E246", {"points": [v(4.49, -35.58) * mm, v(5.14, -35.2) * mm, v(6.83, -35.27) * mm, v(8.82, -35.74) * mm]});
            skFitSpline(sketch, "E247", {"points": [v(8.82, -35.74) * mm, v(9.8, -35.97) * mm, v(10.8, -36.19) * mm, v(11.03, -36.22) * mm]});
            skFitSpline(sketch, "E248", {"points": [v(11.03, -36.22) * mm, v(11.68, -36.3) * mm, v(7.8, -37.2) * mm, v(5.89, -37.42) * mm]});
            skFitSpline(sketch, "E249", {"points": [v(5.89, -37.42) * mm, v(3.88, -37.63) * mm, v(3.44, -37.81) * mm, v(4.5, -37.99) * mm]});
            skFitSpline(sketch, "E250", {"points": [v(4.5, -37.99) * mm, v(4.92, -38.06) * mm, v(5.46, -38.22) * mm, v(5.7, -38.34) * mm]});
            skFitSpline(sketch, "E251", {"points": [v(5.7, -38.34) * mm, v(6.08, -38.55) * mm, v(5.93, -38.58) * mm, v(4.32, -38.58) * mm]});
            skFitSpline(sketch, "E252", {"points": [v(4.32, -38.58) * mm, v(3.32, -38.59) * mm, v(1.66, -38.63) * mm, v(0.62, -38.68) * mm]});
            skFitSpline(sketch, "E253", {"points": [v(0.62, -38.68) * mm, v(-0.42, -38.72) * mm, v(-1.38, -38.71) * mm, v(-1.5, -38.66) * mm]});
            skLineSegment(sketch, "E254", {"start": v(0.46, -34.18) * mm, "end": v(0.1, -34.66) * mm});
            skLineSegment(sketch, "E255", {"start": v(0.1, -34.66) * mm, "end": v(0.5, -34.99) * mm});
            skFitSpline(sketch, "E256", {"points": [v(-12.63, -31.81) * mm, v(-10.55, -31.27) * mm, v(-7.27, -29.68) * mm, v(-5.58, -28.4) * mm]});
            skFitSpline(sketch, "E257", {"points": [v(-5.58, -28.4) * mm, v(-3.4, -26.76) * mm, v(-0.95, -24.05) * mm, v(0.18, -22.04) * mm]});
            skFitSpline(sketch, "E258", {"points": [v(-18.94, -26.8) * mm, v(-19.54, -30.77) * mm, v(-19.7, -32.17) * mm, v(-19.55, -32.27) * mm]});
            skFitSpline(sketch, "E259", {"points": [v(-19.55, -32.27) * mm, v(-19.44, -32.35) * mm, v(-18.22, -32.38) * mm, v(-16.85, -32.34) * mm]});
            skFitSpline(sketch, "E260", {"points": [v(-16.85, -32.34) * mm, v(-14.88, -32.28) * mm, v(-14, -32.17) * mm, v(-12.63, -31.81) * mm]});
            skLineSegment(sketch, "E261", {"start": v(0.18, -22.04) * mm, "end": v(0.55, -21.38) * mm});
            skLineSegment(sketch, "E262", {"start": v(0.55, -21.38) * mm, "end": v(-8.79, -21.42) * mm});
            skLineSegment(sketch, "E263", {"start": v(-8.79, -21.42) * mm, "end": v(-18.13, -21.47) * mm});
            skLineSegment(sketch, "E264", {"start": v(-18.13, -21.47) * mm, "end": v(-18.94, -26.8) * mm});
            skFitSpline(sketch, "E265", {"points": [v(-27.64, -24.78) * mm, v(-27.38, -23.05) * mm, v(-27.17, -21.58) * mm, v(-27.17, -21.5) * mm]});
            skFitSpline(sketch, "E266", {"points": [v(-27.17, -21.5) * mm, v(-27.18, -21.44) * mm, v(-28.26, -21.38) * mm, v(-29.59, -21.38) * mm]});
            skFitSpline(sketch, "E267", {"points": [v(-29.59, -21.38) * mm, v(-31.04, -21.38) * mm, v(-32, -21.45) * mm, v(-32, -21.55) * mm]});
            skFitSpline(sketch, "E268", {"points": [v(-32, -21.55) * mm, v(-32, -21.95) * mm, v(-31.06, -24.14) * mm, v(-30.46, -25.17) * mm]});
            skFitSpline(sketch, "E269", {"points": [v(-30.46, -25.17) * mm, v(-29.8, -26.28) * mm, v(-28.47, -27.92) * mm, v(-28.23, -27.92) * mm]});
            skFitSpline(sketch, "E270", {"points": [v(-28.23, -27.92) * mm, v(-28.16, -27.92) * mm, v(-27.9, -26.5) * mm, v(-27.64, -24.78) * mm]});
            skFitSpline(sketch, "E271", {"points": [v(-26.49, -17.5) * mm, v(-26.49, -17.45) * mm, v(-25.9, -13.56) * mm, v(-25.2, -8.85) * mm]});
            skFitSpline(sketch, "E272", {"points": [v(-25.2, -8.85) * mm, v(-24.48, -4.15) * mm, v(-23.92, -0.14) * mm, v(-23.94, 0.05) * mm]});
            skFitSpline(sketch, "E273", {"points": [v(-23.94, 0.05) * mm, v(-23.98, 0.32) * mm, v(-24.38, 0) * mm, v(-25.9, -1.5) * mm]});
            skFitSpline(sketch, "E274", {"points": [v(-25.9, -1.5) * mm, v(-28.76, -4.34) * mm, v(-30.61, -7.32) * mm, v(-31.72, -10.85) * mm]});
            skFitSpline(sketch, "E275", {"points": [v(-31.72, -10.85) * mm, v(-32.3, -12.7) * mm, v(-32.68, -14.92) * mm, v(-32.68, -16.41) * mm]});
            skFitSpline(sketch, "E276", {"points": [v(-29.59, -17.6) * mm, v(-27.88, -17.6) * mm, v(-26.49, -17.55) * mm, v(-26.49, -17.5) * mm]});
            skLineSegment(sketch, "E277", {"start": v(-32.68, -16.41) * mm, "end": v(-32.68, -17.6) * mm});
            skLineSegment(sketch, "E278", {"start": v(-32.68, -17.6) * mm, "end": v(-29.59, -17.6) * mm});
            skFitSpline(sketch, "E279", {"points": [v(2.56, -16.95) * mm, v(5.46, -7.27) * mm, v(0.91, 1.83) * mm, v(-7.99, 4.18) * mm]});
            skFitSpline(sketch, "E280", {"points": [v(-7.99, 4.18) * mm, v(-9.24, 4.51) * mm, v(-11.97, 4.7) * mm, v(-13.25, 4.54) * mm]});
            skFitSpline(sketch, "E281", {"points": [v(-15.79, -6.29) * mm, v(-16.67, -12.17) * mm, v(-17.43, -17.13) * mm, v(-17.48, -17.3) * mm]});
            skFitSpline(sketch, "E282", {"points": [v(-17.48, -17.3) * mm, v(-17.56, -17.58) * mm, v(-17, -17.6) * mm, v(-7.6, -17.6) * mm]});
            skLineSegment(sketch, "E283", {"start": v(-13.25, 4.54) * mm, "end": v(-14.18, 4.42) * mm});
            skLineSegment(sketch, "E284", {"start": v(-14.18, 4.42) * mm, "end": v(-15.79, -6.29) * mm});
            skLineSegment(sketch, "E285", {"start": v(-7.6, -17.6) * mm, "end": v(2.37, -17.6) * mm});
            skLineSegment(sketch, "E286", {"start": v(2.37, -17.6) * mm, "end": v(2.56, -16.95) * mm});
            skSolve(sketch);
        }
        {
            var Q0;
            Q0 = qSketchRegion(id + "F0", true);
            extrude(context, id + "F1", {"entities" : qUnion([Q0]), "depth" : .4 * mm, "offsetDistance" : 25 * mm});
        }
    });
